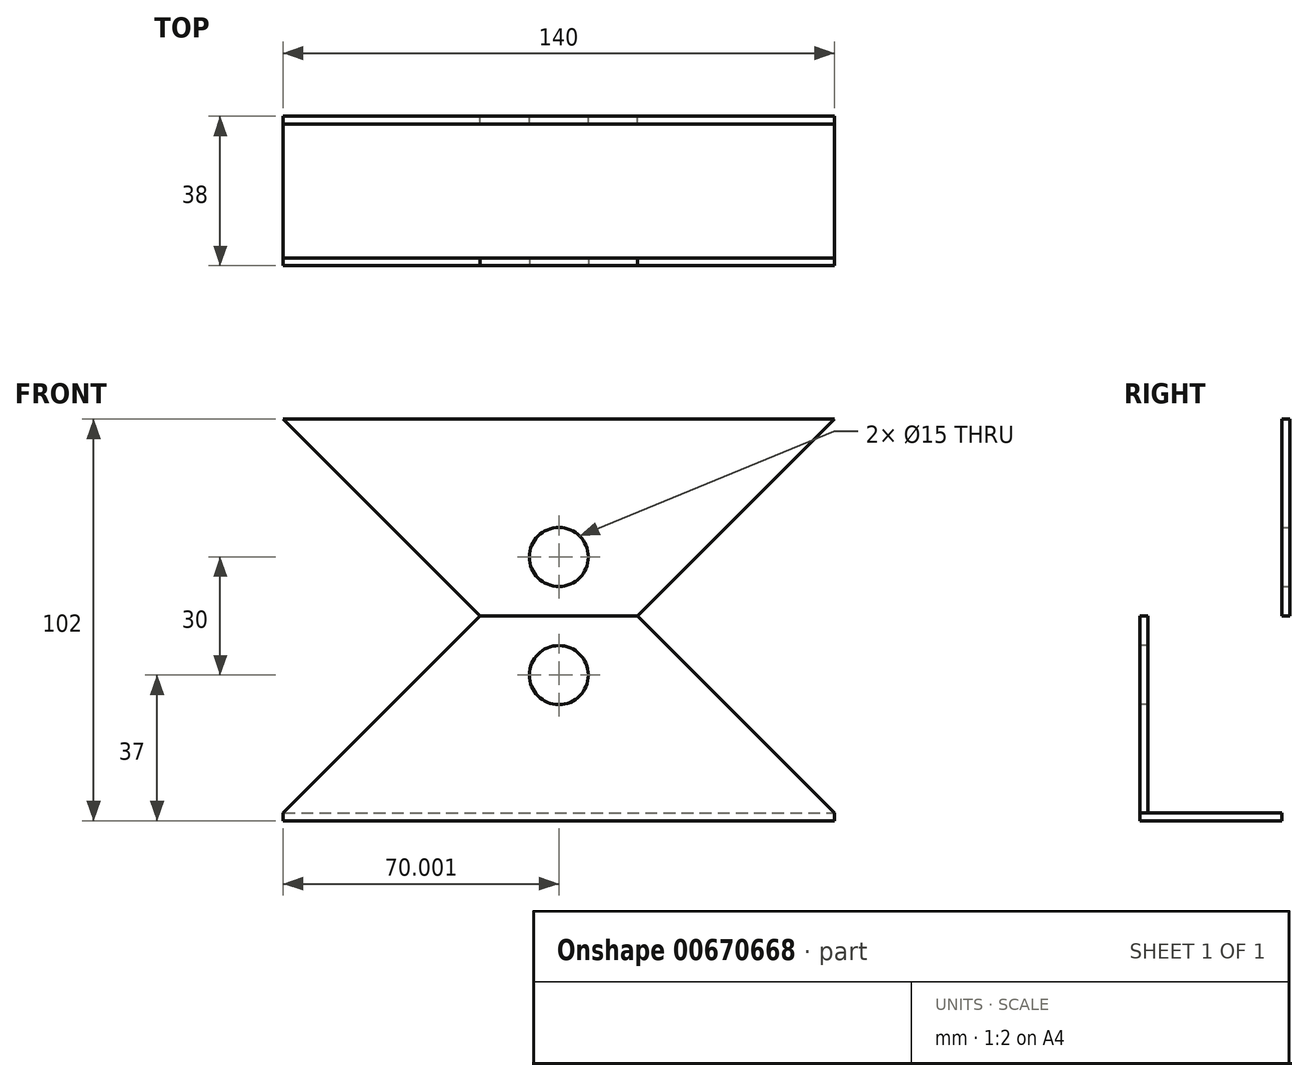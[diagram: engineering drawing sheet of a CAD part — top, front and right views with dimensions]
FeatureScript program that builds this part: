
annotation { "Feature Type Name" : "Feature", "Feature Type Description" : "" }
export const myFeature = defineFeature(function(context is Context, id is Id, definition is map)
    precondition{}
    {
        {
            var Q0;
            Q0=qCreatedBy(makeId("Front.planeOp"),FACE);
            var sketch = newSketch(context, id + "F0", { "sketchPlane" : qUnion([Q0])});
            skLineSegment(sketch, "E0.bottom", {"start": v(-70.18, 37.3) * mm, "end": v(69.82, 37.3) * mm});
            skLineSegment(sketch, "E0.top", {"start": v(-70.18, 35.3) * mm, "end": v(69.82, 35.3) * mm});
            skLineSegment(sketch, "E0.left", {"start": v(-70.18, 37.3) * mm, "end": v(-70.18, 35.3) * mm});
            skLineSegment(sketch, "E0.right", {"start": v(69.82, 37.3) * mm, "end": v(69.82, 35.3) * mm});
            skCircle(sketch, "E1", {"center": v(-0.18, 0.3) * mm, "radius": 7.5 * mm});
            skLineSegment(sketch, "E2", {"start": v(-20.18, -14.7) * mm, "end": v(-70.18, 35.3) * mm});
            skLineSegment(sketch, "E3", {"start": v(-20.18, -14.7) * mm, "end": v(19.82, -14.7) * mm});
            skLineSegment(sketch, "E4", {"start": v(19.82, -14.7) * mm, "end": v(69.82, 35.3) * mm});
            skSolve(sketch);
        }
        {
            var Q0;
            Q0=makeQuery(id+"F0.imprint","IMPRINT",FACE,{"disambiguationData":[TD([[makeQuery(id+"F0.imprint","IMPRINT",EDGE,{"derivedFrom":sQuery(id+"F0.wireOp",EDGE,"E0.top")}),-1.0]])]});
            extrude(context, id + "F1", {"entities" : qUnion([Q0]), "depth" : 2 * mm, "offsetDistance" : 25 * mm});
        }
        {
            var Q0;
            Q0=makeQuery(id+"F0.imprint","IMPRINT",FACE,{"disambiguationData":[TD([[makeQuery(id+"F0.imprint","IMPRINT",EDGE,{"derivedFrom":sQuery(id+"F0.wireOp",EDGE,"E0.bottom")}),-1.0]])]});
            extrude(context, id + "F2", {"entities" : qUnion([Q0]), "operationType" : NewBodyOperationType.ADD, "depth" : 36 * mm, "offsetDistance" : 25 * mm});
        }
        {
            var Q0;
            Q0=makeQuery(id+"F0.imprint","IMPRINT",FACE,{"disambiguationData":[TD([[makeQuery(id+"F0.imprint","IMPRINT",EDGE,{"derivedFrom":sQuery(id+"F0.wireOp",EDGE,"E0.top")}),-1.0]])]});
            extrude(context, id + "F3", {"entities" : qUnion([Q0]), "depth" : 2 * mm, "offsetDistance" : 25 * mm});
        }
        {
            var Q0;
            Q0=makeQuery(id+"F3.opExtrude","SWEPT_BODY",BODY,{"disambiguationData":[OSD([sQuery(id+"F0.wireOp",EDGE,"E0.top"),sQuery(id+"F0.wireOp",EDGE,"E1"),sQuery(id+"F0.wireOp",EDGE,"E2"),sQuery(id+"F0.wireOp",EDGE,"E3"),sQuery(id+"F0.wireOp",EDGE,"E4")])]});
            transform(context, id + "F4", {"entities" : qUnion([Q0]), "transformType" : TransformType.TRANSLATION_3D, "dx" : 0 * mm, "dy" : -34 * mm, "dz" : 0 * mm, "makeCopy" : false});
        }
        {
            var Q0;
            Q0=makeQuery(id+"F1.opExtrude","SWEPT_BODY",BODY,{"disambiguationData":[OSD([sQuery(id+"F0.wireOp",EDGE,"E0.top"),sQuery(id+"F0.wireOp",EDGE,"E1"),sQuery(id+"F0.wireOp",EDGE,"E2"),sQuery(id+"F0.wireOp",EDGE,"E3"),sQuery(id+"F0.wireOp",EDGE,"E4")])]});
            var Q1;
            Q1=makeQuery(id+"F3.opExtrude","CAP_EDGE",EDGE,{"disambiguationData":[OSD([sQuery(id+"F0.wireOp",EDGE,"E3")])],"isStart":false});
            transform(context, id + "F5", {"entities" : qUnion([Q0]), "transformType" : TransformType.ROTATION, "transformAxis" : qUnion([Q1]), "angle" : 180 * degree, "makeCopy" : false});
        }
    });
